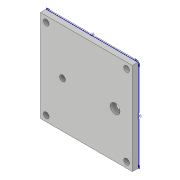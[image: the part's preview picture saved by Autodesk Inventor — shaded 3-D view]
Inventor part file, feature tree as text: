
AUTODESK INVENTOR PART (.ipt)
format: ipt  version: 2019 (Build 230136000, 136)  size: 107,520 bytes
history: native  units: mm
features: extrude x3, sketch x3
ambient origin geometry x8: Origin, YZ Plane, XZ Plane, XY Plane, X Axis, Y Axis, Z Axis, Center Point
bodies: Solid1 (feature_tree)
feature tree (6):
  extrude  "Extrusion1"  Depth=160.0mm
  sketch  "Sketch2"  dims[d2=10.0mm d3=0.0mm d4=10.0mm]
  extrude  "Extrusion2"  Depth=10.0mm
  extrude  "Extrusion3"  Depth=10.0mm
  sketch  "Sketch1"  dims[d0=160.0mm d1=160.0mm]
  sketch  "Sketch3"  dims[d5=150.0mm d6=140.0mm d7=140.0mm d8=38.5mm d9=80.0mm d10=38.5mm d11=10.0mm d12=80.0mm d13=30.0mm d14=17.0mm d15=10.0mm d16=10.0mm d17=10.0mm d18=10.0mm d19=0.0mm d20=0.0mm d21=0.0mm d22=0.0mm]
